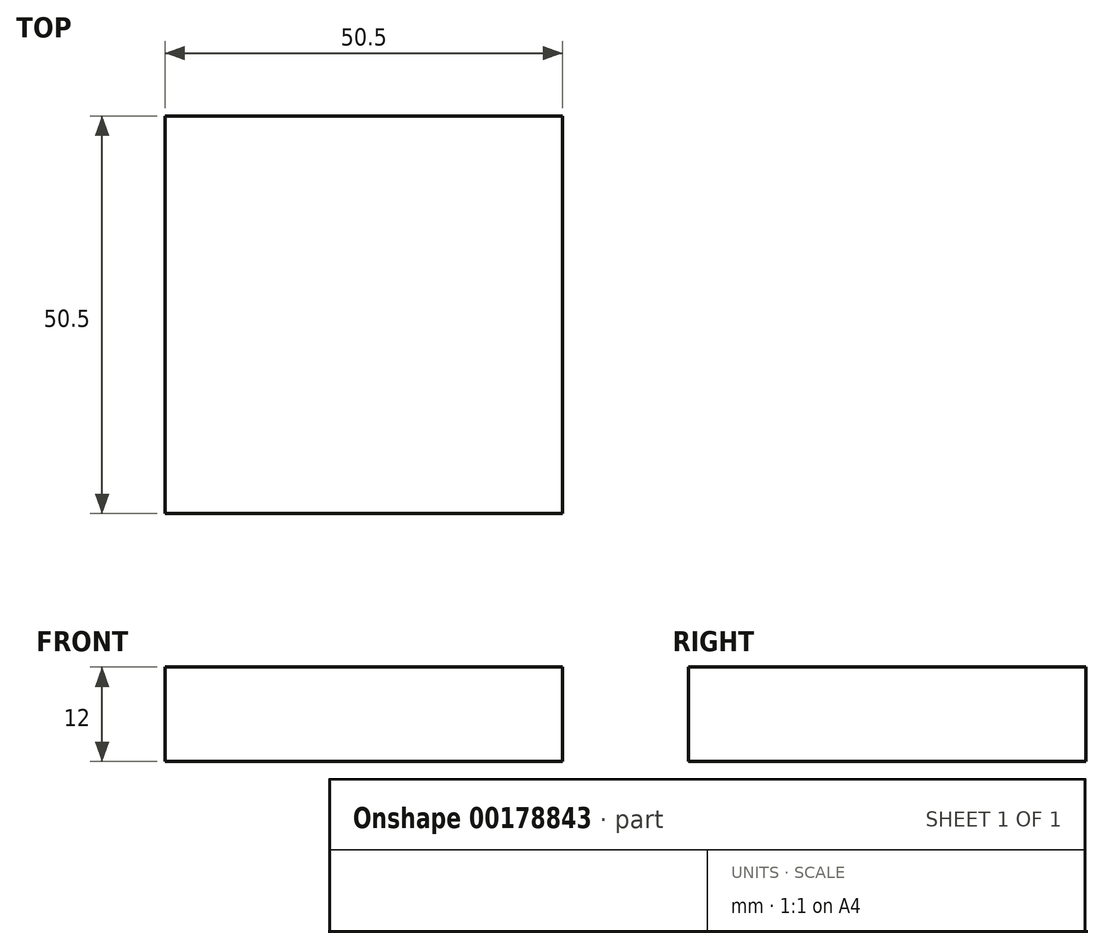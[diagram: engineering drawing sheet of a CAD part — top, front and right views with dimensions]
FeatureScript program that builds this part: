
annotation { "Feature Type Name" : "Feature", "Feature Type Description" : "" }
export const myFeature = defineFeature(function(context is Context, id is Id, definition is map)
    precondition{}
    {
        {
            var Q0;
            Q0=qCreatedBy(makeId("Top.planeOp"),FACE);
            var sketch = newSketch(context, id + "F0", { "sketchPlane" : qUnion([Q0])});
            skLineSegment(sketch, "E0.bottom", {"start": v(-25.25, 25.25) * mm, "end": v(25.25, 25.25) * mm});
            skLineSegment(sketch, "E0.top", {"start": v(-25.25, -25.25) * mm, "end": v(25.25, -25.25) * mm});
            skLineSegment(sketch, "E0.left", {"start": v(-25.25, 25.25) * mm, "end": v(-25.25, -25.25) * mm});
            skLineSegment(sketch, "E0.right", {"start": v(25.25, 25.25) * mm, "end": v(25.25, -25.25) * mm});
            skLineSegment(sketch, "E1", {"start": v(-25.25, 25.25) * mm, "end": v(25.25, -25.25) * mm, "construction": true});
            skPoint(sketch, "E2", {"position": v(0, 0) * mm});
            skSolve(sketch);
        }
        {
            var Q0;
            Q0=makeQuery(id+"F0.imprint","IMPRINT",FACE,{"disambiguationData":[TD([[makeQuery(id+"F0.imprint","IMPRINT",EDGE,{"derivedFrom":sQuery(id+"F0.wireOp",EDGE,"E0.bottom")}),-1.0]])]});
            extrude(context, id + "F1", {"entities" : qUnion([Q0]), "depth" : 12 * mm});
        }
    });
